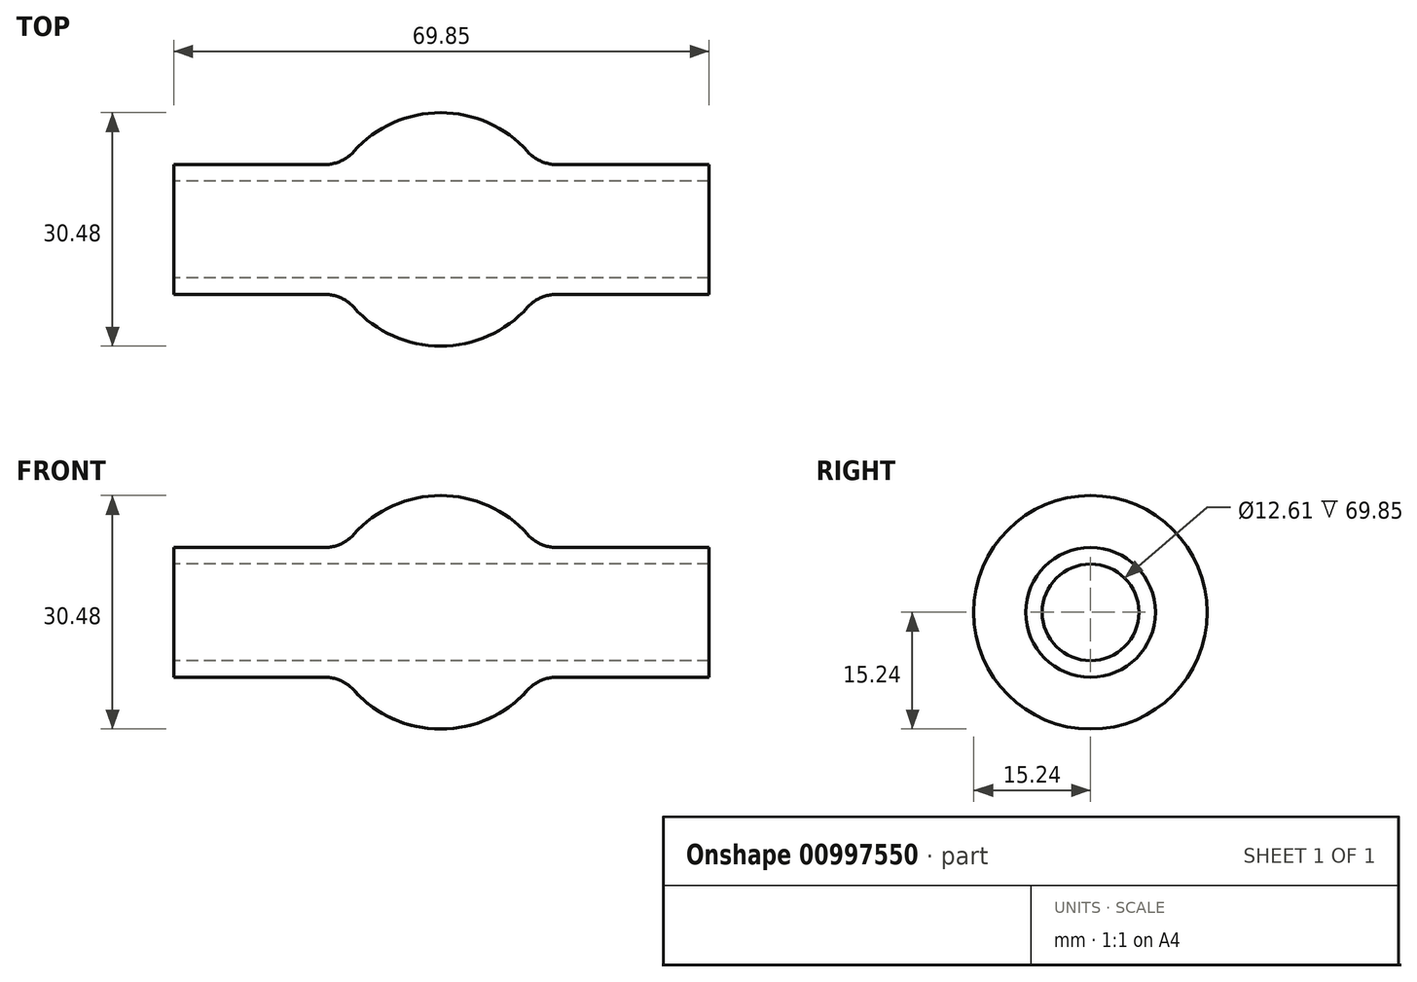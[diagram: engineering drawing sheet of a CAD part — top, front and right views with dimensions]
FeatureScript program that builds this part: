
annotation { "Feature Type Name" : "Feature", "Feature Type Description" : "" }
export const myFeature = defineFeature(function(context is Context, id is Id, definition is map)
    precondition{}
    {
        {
            var Q0;
            Q0=qCreatedBy(makeId("Front.planeOp"),FACE);
            var sketch = newSketch(context, id + "F0", { "sketchPlane" : qUnion([Q0])});
            skLineSegment(sketch, "E0", {"start": v(0.1, -6.3) * mm, "end": v(35.02, -6.3) * mm});
            skLineSegment(sketch, "E1", {"start": v(0.1, -6.3) * mm, "end": v(-34.83, -6.3) * mm});
            skLineSegment(sketch, "E2", {"start": v(-34.83, -6.3) * mm, "end": v(-34.83, -8.47) * mm});
            skLineSegment(sketch, "E3", {"start": v(35.02, -6.3) * mm, "end": v(35.02, -8.47) * mm});
            skPoint(sketch, "E4", {"position": v(-12.7, 0) * mm});
            skPoint(sketch, "E5", {"position": v(12.7, 0) * mm});
            skPoint(sketch, "E6", {"position": v(-13.87, -6.3) * mm});
            skPoint(sketch, "E7", {"position": v(14.07, -6.3) * mm});
            skLineSegment(sketch, "E8", {"start": v(-12.7, 0) * mm, "end": v(12.7, 0) * mm});
            skArc(sketch, "E9", {"start": v(-13.87, -6.3) * mm, "mid": v(0, -15.24) * mm, "end": v(13.87, -6.3) * mm});
            skLineSegment(sketch, "E10", {"start": v(-34.83, -8.47) * mm, "end": v(35.02, -8.47) * mm});
            skSolve(sketch);
        }
        {
            var Q0;
            {var subQ1=sQuery(id+"F0.wireOp",EDGE,"E1");var subQ5=sQuery(id+"F0.wireOp",EDGE,"E0");var subQ6=makeQuery(id+"F0.imprint","INTERSECT",VERTEX,{"derivedFrom":[subQ5,subQ1]});Q0=makeQuery(id+"F0.imprint","IMPRINT",FACE,{"disambiguationData":[TD([[makeQuery(id+"F0.imprint","IMPRINT",EDGE,{"disambiguationData":[TD([[subQ6,-1.0]])],"derivedFrom":subQ5}),-1.0]])]});}
            var Q1;
            {var subQ0=sQuery(id+"F0.wireOp",EDGE,"E2");Q1=makeQuery(id+"F0.imprint","IMPRINT",FACE,{"disambiguationData":[TD([[makeQuery(id+"F0.imprint","IMPRINT",EDGE,{"derivedFrom":subQ0}),1.0]])]});}
            var Q2;
            {var subQ0=sQuery(id+"F0.wireOp",EDGE,"E3");Q2=makeQuery(id+"F0.imprint","IMPRINT",FACE,{"disambiguationData":[TD([[makeQuery(id+"F0.imprint","IMPRINT",EDGE,{"derivedFrom":subQ0}),-1.0]])]});}
            var Q3;
            {var subQ0=sQuery(id+"F0.wireOp",EDGE,"E10");var subQ1=sQuery(id+"F0.wireOp",EDGE,"E9");var subQ2=makeQuery(id+"F0.imprint","INTERSECT",VERTEX,{"disambiguationData":[OD(0.0)],"derivedFrom":[subQ1,subQ0]});Q3=makeQuery(id+"F0.imprint","IMPRINT",FACE,{"disambiguationData":[TD([[makeQuery(id+"F0.imprint","IMPRINT",EDGE,{"disambiguationData":[TD([[subQ2,-1.0]])],"derivedFrom":subQ1}),1.0]])]});}
            var Q4;
            Q4=sQuery(id+"F0.wireOp",EDGE,"E8");
            revolve(context, id + "F1", {"surfaceOperationType" : NewSurfaceOperationType.NEW, "entities" : qUnion([Q0, Q1, Q2, Q3]), "axis" : qUnion([Q4]), "revolveType" : RevolveType.FULL});
        }
        {
            var Q0;
            {var subQ0=sQuery(id+"F0.wireOp",EDGE,"E10");var subQ1=sQuery(id+"F0.wireOp",EDGE,"E9");Q0=makeQuery(id+"F1.opRevolve","SWEPT_EDGE",EDGE,{"disambiguationData":[OSD([subQ1,subQ0]),TDD([makeQuery(id+"F0.imprint","INTERSECT",VERTEX,{"disambiguationData":[OD(0.0)],"derivedFrom":[subQ1,subQ0]})])]});}
            var Q1;
            {var subQ0=sQuery(id+"F0.wireOp",EDGE,"E10");var subQ1=sQuery(id+"F0.wireOp",EDGE,"E9");Q1=makeQuery(id+"F1.opRevolve","SWEPT_EDGE",EDGE,{"disambiguationData":[OSD([subQ1,subQ0]),TDD([makeQuery(id+"F0.imprint","INTERSECT",VERTEX,{"disambiguationData":[OD(1.0)],"derivedFrom":[subQ1,subQ0]})])]});}
            fillet(context, id + "F2", {"entities" : qUnion([Q0, Q1]), "radius" : 5.08 * mm, "tangentPropagation" : true, "allowEdgeOverflow" : false});
        }
    });
